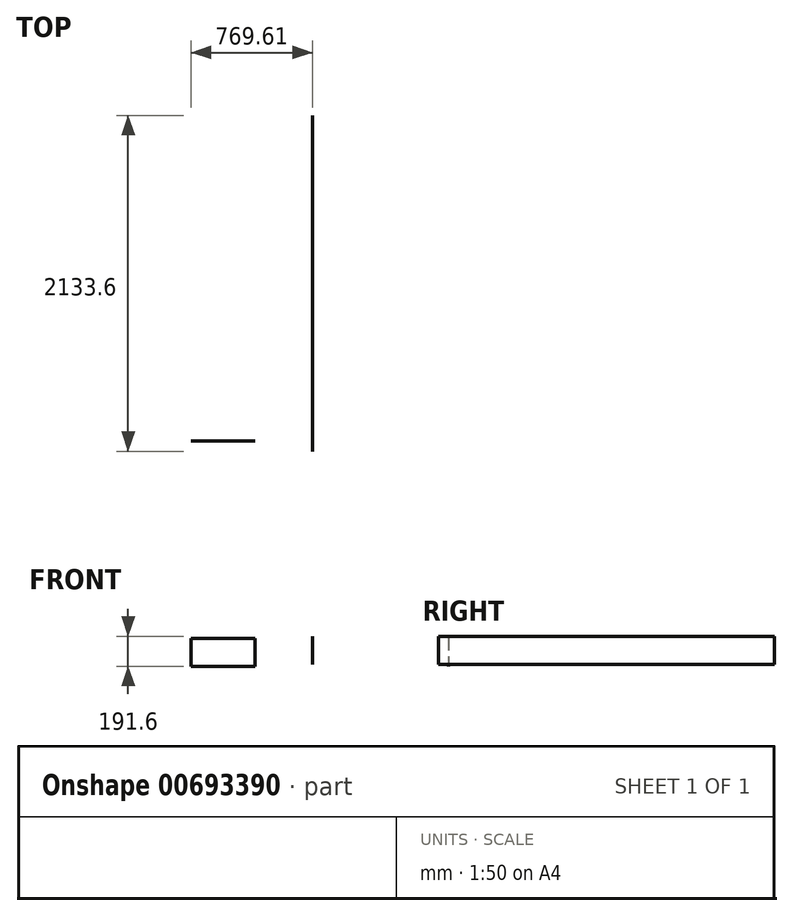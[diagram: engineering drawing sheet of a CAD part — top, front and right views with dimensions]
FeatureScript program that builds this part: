
annotation { "Feature Type Name" : "Feature", "Feature Type Description" : "" }
export const myFeature = defineFeature(function(context is Context, id is Id, definition is map)
    precondition{}
    {
        {
            assignVariable(context, id + "F0", {"name" : "T", "anyValue" : .5});
        }
        {
            var Q0;
            Q0=qCreatedBy(makeId("Right.planeOp"),FACE);
            var sketch = newSketch(context, id + "F1", { "sketchPlane" : qUnion([Q0])});
            skLineSegment(sketch, "E0.bottom", {"start": v(-64.65, 191.6) * mm, "end": v(2068.95, 191.6) * mm});
            skLineSegment(sketch, "E0.top", {"start": v(-64.65, 13.8) * mm, "end": v(2068.95, 13.8) * mm});
            skLineSegment(sketch, "E0.left", {"start": v(-64.65, 191.6) * mm, "end": v(-64.65, 13.8) * mm});
            skLineSegment(sketch, "E0.right", {"start": v(2068.95, 191.6) * mm, "end": v(2068.95, 13.8) * mm});
            skSolve(sketch);
        }
        {
            var Q0;
            Q0 = qSketchRegion(id + "F1", true);
            extrude(context, id + "F2", {"entities" : qUnion([Q0]), "depth" : (getVariable(context, 'T')) * mm, "offsetDistance" : 25.4 * mm});
        }
        {
            var Q0;
            Q0=qCreatedBy(makeId("Front.planeOp"),FACE);
            var sketch = newSketch(context, id + "F3", { "sketchPlane" : qUnion([Q0])});
            skLineSegment(sketch, "E1.bottom", {"start": v(-769.1, 177.8) * mm, "end": v(-362.7, 177.8) * mm});
            skLineSegment(sketch, "E1.top", {"start": v(-769.1, 0) * mm, "end": v(-362.7, 0) * mm});
            skLineSegment(sketch, "E1.left", {"start": v(-769.1, 177.8) * mm, "end": v(-769.1, 0) * mm});
            skLineSegment(sketch, "E1.right", {"start": v(-362.7, 177.8) * mm, "end": v(-362.7, 0) * mm});
            skSolve(sketch);
        }
        {
            var Q0;
            Q0 = qSketchRegion(id + "F3", true);
            extrude(context, id + "F4", {"entities" : qUnion([Q0]), "depth" : (getVariable(context, 'T')) * mm, "offsetDistance" : 25.4 * mm});
        }
    });
